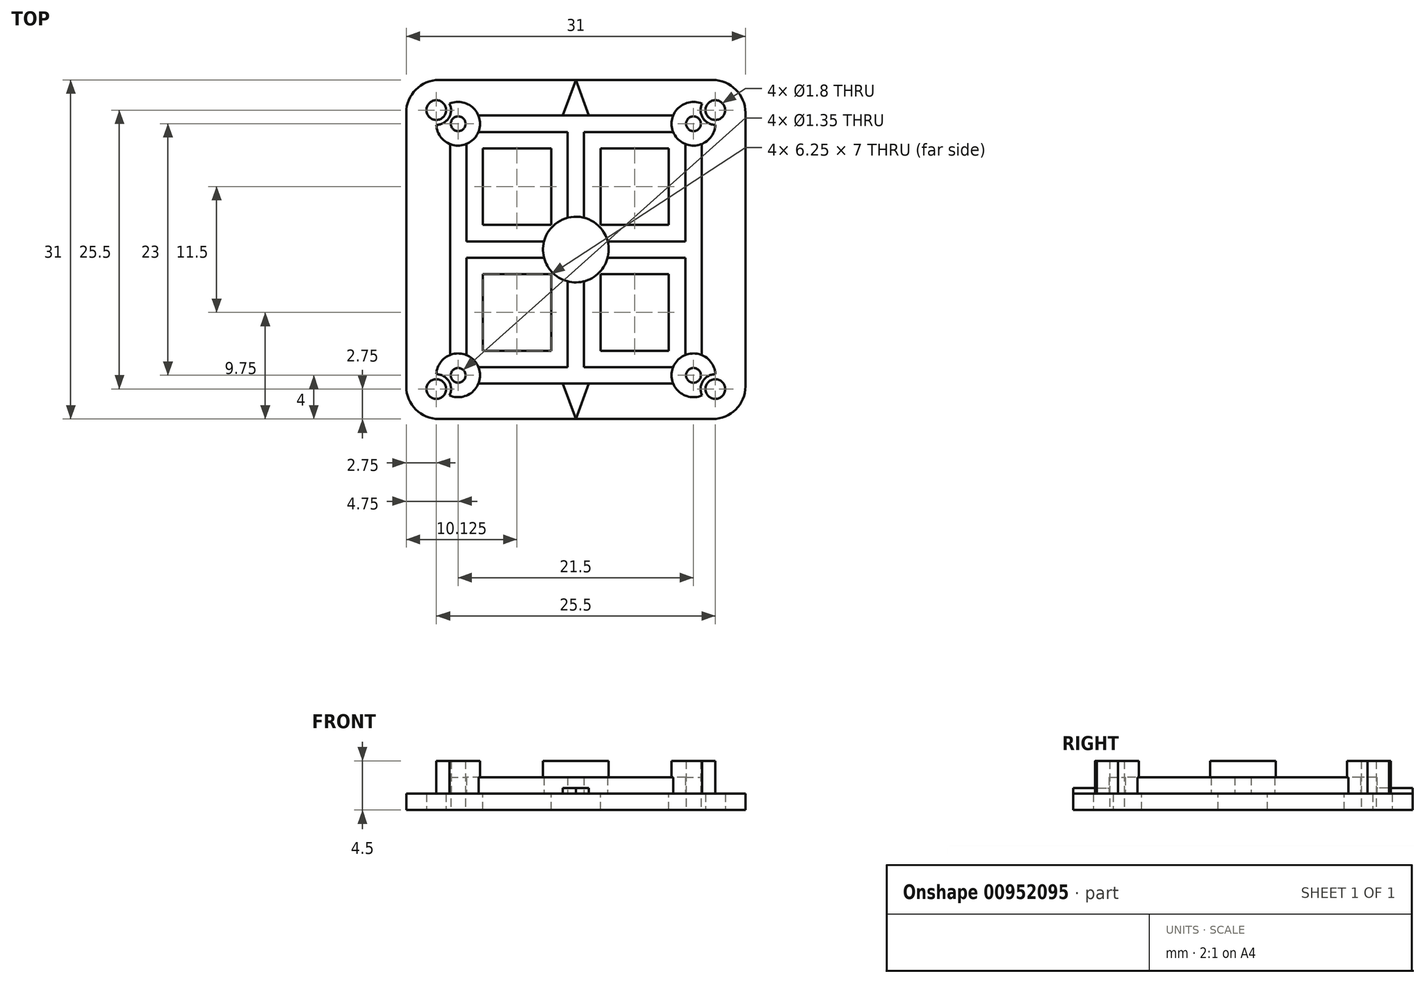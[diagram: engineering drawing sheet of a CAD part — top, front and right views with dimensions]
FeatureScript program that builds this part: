
annotation { "Feature Type Name" : "Feature", "Feature Type Description" : "" }
export const myFeature = defineFeature(function(context is Context, id is Id, definition is map)
    precondition{}
    {
        {
            var Q0;
            Q0=qCreatedBy(makeId("Top.planeOp"),FACE);
            var sketch = newSketch(context, id + "F0", { "sketchPlane" : qUnion([Q0])});
            skCircle(sketch, "E0", {"center": v(-12.75, 12.75) * mm, "radius": 0.9 * mm});
            skCircle(sketch, "E1.MirrorC", {"center": v(12.75, 12.75) * mm, "radius": 0.9 * mm});
            skCircle(sketch, "E2.MirrorC", {"center": v(12.75, -12.75) * mm, "radius": 0.9 * mm});
            skCircle(sketch, "E3.MirrorC", {"center": v(-12.75, -12.75) * mm, "radius": 0.9 * mm});
            skLineSegment(sketch, "E4.bottom", {"start": v(-15.5, 15.5) * mm, "end": v(15.5, 15.5) * mm});
            skLineSegment(sketch, "E4.top", {"start": v(-15.5, -15.5) * mm, "end": v(15.5, -15.5) * mm});
            skLineSegment(sketch, "E4.left", {"start": v(-15.5, 15.5) * mm, "end": v(-15.5, -15.5) * mm});
            skLineSegment(sketch, "E4.right", {"start": v(15.5, 15.5) * mm, "end": v(15.5, -15.5) * mm});
            skSolve(sketch);
        }
        {
            var Q0;
            Q0 = qSketchRegion(id + "F0", true);
            extrude(context, id + "F1", {"entities" : qUnion([Q0]), "depth" : 1.5 * mm, "offsetDistance" : 25 * mm});
        }
        {
            var Q0;
            Q0=makeQuery(id+"F1.opExtrude","CAP_FACE",FACE,{"disambiguationData":[OSD([sQuery(id+"F0.wireOp",EDGE,"E0"),sQuery(id+"F0.wireOp",EDGE,"E1.MirrorC"),sQuery(id+"F0.wireOp",EDGE,"E2.MirrorC"),sQuery(id+"F0.wireOp",EDGE,"E3.MirrorC"),sQuery(id+"F0.wireOp",EDGE,"E4.bottom"),sQuery(id+"F0.wireOp",EDGE,"E4.top"),sQuery(id+"F0.wireOp",EDGE,"E4.left"),sQuery(id+"F0.wireOp",EDGE,"E4.right")])],"isStart":false});
            var sketch = newSketch(context, id + "F2", { "sketchPlane" : qUnion([Q0])});
            skCircle(sketch, "E5", {"center": v(10.75, 11.5) * mm, "radius": 0.68 * mm});
            skCircle(sketch, "E6.MirrorC", {"center": v(-10.75, 11.5) * mm, "radius": 0.68 * mm});
            skCircle(sketch, "E7.MirrorC", {"center": v(-10.75, -11.5) * mm, "radius": 0.68 * mm});
            skCircle(sketch, "E8.MirrorC", {"center": v(10.75, -11.5) * mm, "radius": 0.68 * mm});
            skCircle(sketch, "E9", {"center": v(-10.75, 11.5) * mm, "radius": 2 * mm});
            skCircle(sketch, "E10.MirrorC", {"center": v(10.75, 11.5) * mm, "radius": 2 * mm});
            skCircle(sketch, "E11.MirrorC", {"center": v(10.75, -11.5) * mm, "radius": 2 * mm});
            skCircle(sketch, "E12.MirrorC", {"center": v(-10.75, -11.5) * mm, "radius": 2 * mm});
            skSolve(sketch);
        }
        {
            var Q0;
            Q0 = qSketchRegion(id + "F2", true);
            extrude(context, id + "F3", {"entities" : qUnion([Q0]), "operationType" : NewBodyOperationType.ADD, "depth" : 3 * mm, "offsetDistance" : 25 * mm});
        }
        {
            var Q0;
            Q0=makeQuery(id+"F1.opExtrude","SWEPT_EDGE",EDGE,{"disambiguationData":[OSD([sQuery(id+"F0.wireOp",EDGE,"E4.bottom"),sQuery(id+"F0.wireOp",EDGE,"E4.left")])]});
            var Q1;
            Q1=makeQuery(id+"F1.opExtrude","SWEPT_EDGE",EDGE,{"disambiguationData":[OSD([sQuery(id+"F0.wireOp",EDGE,"E4.bottom"),sQuery(id+"F0.wireOp",EDGE,"E4.right")])]});
            var Q2;
            Q2=makeQuery(id+"F1.opExtrude","SWEPT_EDGE",EDGE,{"disambiguationData":[OSD([sQuery(id+"F0.wireOp",EDGE,"E4.top"),sQuery(id+"F0.wireOp",EDGE,"E4.right")])]});
            var Q3;
            Q3=makeQuery(id+"F1.opExtrude","SWEPT_EDGE",EDGE,{"disambiguationData":[OSD([sQuery(id+"F0.wireOp",EDGE,"E4.top"),sQuery(id+"F0.wireOp",EDGE,"E4.left")])]});
            fillet(context, id + "F4", {"entities" : qUnion([Q0, Q1, Q2, Q3]), "radius" : 3 * mm, "tangentPropagation" : true, "allowEdgeOverflow" : false});
        }
        {
            var Q0;
            {var subQ1=sQuery(id+"F0.wireOp",EDGE,"E3.MirrorC");var subQ2=sQuery(id+"F0.wireOp",EDGE,"E4.right");var subQ3=sQuery(id+"F0.wireOp",EDGE,"E4.left");var subQ5=sQuery(id+"F0.wireOp",EDGE,"E4.top");var subQ6=sQuery(id+"F0.wireOp",EDGE,"E4.bottom");var subQ7=sQuery(id+"F0.wireOp",EDGE,"E0");var subQ8=sQuery(id+"F0.wireOp",EDGE,"E1.MirrorC");var subQ9=sQuery(id+"F0.wireOp",EDGE,"E2.MirrorC");Q0=makeQuery(id+"F3.boolean.opBoolean","SPLIT",FACE,{"disambiguationData":[TD([makeQuery(id+"F1.opExtrude","SWEPT_FACE",FACE,{"disambiguationData":[OSD([subQ7])]})])],"derivedFrom":makeQuery(id+"F1.opExtrude","CAP_FACE",FACE,{"disambiguationData":[OSD([subQ7,subQ8,subQ9,subQ1,subQ6,subQ5,subQ3,subQ2])],"isStart":false})});}
            var sketch = newSketch(context, id + "F5", { "sketchPlane" : qUnion([Q0])});
            skLineSegment(sketch, "E13.bottom", {"start": v(-8.9, -10.75) * mm, "end": v(8.9, -10.75) * mm});
            skLineSegment(sketch, "E13.top", {"start": v(-8.9, -12.25) * mm, "end": v(8.9, -12.25) * mm});
            skLineSegment(sketch, "E13.left", {"start": v(-8.9, -10.75) * mm, "end": v(-8.9, -12.25) * mm});
            skLineSegment(sketch, "E13.right", {"start": v(8.9, -10.75) * mm, "end": v(8.9, -12.25) * mm});
            skLineSegment(sketch, "E14.bottom", {"start": v(-8.9, 12.25) * mm, "end": v(8.9, 12.25) * mm});
            skLineSegment(sketch, "E14.top", {"start": v(-8.9, 10.75) * mm, "end": v(8.9, 10.75) * mm});
            skLineSegment(sketch, "E14.left", {"start": v(-8.9, 12.25) * mm, "end": v(-8.9, 10.75) * mm});
            skLineSegment(sketch, "E14.right", {"start": v(8.9, 12.25) * mm, "end": v(8.9, 10.75) * mm});
            skLineSegment(sketch, "E15.bottom", {"start": v(-11.5, 9.65) * mm, "end": v(-10, 9.65) * mm});
            skLineSegment(sketch, "E15.top", {"start": v(-11.5, -9.65) * mm, "end": v(-10, -9.65) * mm});
            skLineSegment(sketch, "E15.left", {"start": v(-11.5, 9.65) * mm, "end": v(-11.5, -9.65) * mm});
            skLineSegment(sketch, "E15.right", {"start": v(-10, 9.65) * mm, "end": v(-10, -9.65) * mm});
            skLineSegment(sketch, "E16.MirrorCS", {"start": v(10, 9.65) * mm, "end": v(10, -9.65) * mm});
            skLineSegment(sketch, "E17.MirrorCS", {"start": v(11.5, 9.65) * mm, "end": v(11.5, -9.65) * mm});
            skLineSegment(sketch, "E18.MirrorCS", {"start": v(11.5, -9.65) * mm, "end": v(10, -9.65) * mm});
            skLineSegment(sketch, "E19.MirrorCS", {"start": v(11.5, 9.65) * mm, "end": v(10, 9.65) * mm});
            skLineSegment(sketch, "E20.bottom", {"start": v(-0.75, 10.75) * mm, "end": v(0.75, 10.75) * mm});
            skLineSegment(sketch, "E20.top", {"start": v(-0.75, -10.75) * mm, "end": v(0.75, -10.75) * mm});
            skLineSegment(sketch, "E20.left", {"start": v(-0.75, 10.75) * mm, "end": v(-0.75, 0.75) * mm});
            skLineSegment(sketch, "E20.right", {"start": v(0.75, 10.75) * mm, "end": v(0.75, 0.75) * mm});
            skLineSegment(sketch, "E21", {"start": v(-0.75, 0.75) * mm, "end": v(-10, 0.75) * mm});
            skLineSegment(sketch, "E22", {"start": v(-10, 0.75) * mm, "end": v(-10, -0.75) * mm});
            skLineSegment(sketch, "E23", {"start": v(-10, -0.75) * mm, "end": v(-0.75, -0.75) * mm});
            skLineSegment(sketch, "E24.MirrorCS", {"start": v(10, 0.75) * mm, "end": v(10, -0.75) * mm});
            skLineSegment(sketch, "E25.MirrorCS", {"start": v(0.75, 0.75) * mm, "end": v(10, 0.75) * mm});
            skLineSegment(sketch, "E26.MirrorCS", {"start": v(10, -0.75) * mm, "end": v(0.75, -0.75) * mm});
            skLineSegment(sketch, "E27.trimOffspring", {"start": v(-0.75, -0.75) * mm, "end": v(-0.75, -10.75) * mm});
            skLineSegment(sketch, "E28.trimOffspring", {"start": v(0.75, -0.75) * mm, "end": v(0.75, -10.75) * mm});
            skSolve(sketch);
        }
        {
            var Q0;
            Q0 = qSketchRegion(id + "F5", true);
            extrude(context, id + "F6", {"entities" : qUnion([Q0]), "operationType" : NewBodyOperationType.ADD, "depth" : 1.5 * mm, "offsetDistance" : 25 * mm});
        }
        {
            var Q0;
            {var subQ1=sQuery(id+"F0.wireOp",EDGE,"E4.right");var subQ2=sQuery(id+"F0.wireOp",EDGE,"E4.left");var subQ3=sQuery(id+"F0.wireOp",EDGE,"E4.top");var subQ4=sQuery(id+"F0.wireOp",EDGE,"E4.bottom");var subQ5=sQuery(id+"F0.wireOp",EDGE,"E3.MirrorC");var subQ6=sQuery(id+"F0.wireOp",EDGE,"E2.MirrorC");var subQ7=sQuery(id+"F0.wireOp",EDGE,"E1.MirrorC");var subQ8=sQuery(id+"F0.wireOp",EDGE,"E0");var subQ9=makeQuery(id+"F1.opExtrude","CAP_FACE",FACE,{"disambiguationData":[OSD([subQ8,subQ7,subQ6,subQ5,subQ4,subQ3,subQ2,subQ1])],"isStart":false});var subQ15=sQuery(id+"F5.wireOp",EDGE,"E20.left");Q0=makeQuery(id+"F6.boolean.opBoolean","SPLIT",FACE,{"disambiguationData":[TD([makeQuery(id+"F6.opExtrude","SWEPT_FACE",FACE,{"disambiguationData":[OSD([subQ15])]})])],"derivedFrom":makeQuery(id+"F3.boolean.opBoolean","SPLIT",FACE,{"disambiguationData":[TD([makeQuery(id+"F1.opExtrude","SWEPT_FACE",FACE,{"disambiguationData":[OSD([subQ8])]})])],"derivedFrom":subQ9})});}
            var sketch = newSketch(context, id + "F7", { "sketchPlane" : qUnion([Q0])});
            skLineSegment(sketch, "E29.bottom", {"start": v(-8.5, 9.25) * mm, "end": v(-2.25, 9.25) * mm});
            skLineSegment(sketch, "E29.top", {"start": v(-8.5, 2.25) * mm, "end": v(-2.25, 2.25) * mm});
            skLineSegment(sketch, "E29.left", {"start": v(-8.5, 9.25) * mm, "end": v(-8.5, 2.25) * mm});
            skLineSegment(sketch, "E29.right", {"start": v(-2.25, 9.25) * mm, "end": v(-2.25, 2.25) * mm});
            skLineSegment(sketch, "E30.MirrorCS", {"start": v(8.5, 9.25) * mm, "end": v(2.25, 9.25) * mm});
            skLineSegment(sketch, "E31.MirrorCS", {"start": v(8.5, 9.25) * mm, "end": v(8.5, 2.25) * mm});
            skLineSegment(sketch, "E32.MirrorCS", {"start": v(8.5, 2.25) * mm, "end": v(2.25, 2.25) * mm});
            skLineSegment(sketch, "E33.MirrorCS", {"start": v(2.25, 9.25) * mm, "end": v(2.25, 2.25) * mm});
            skLineSegment(sketch, "E34.MirrorCS", {"start": v(2.25, -9.25) * mm, "end": v(2.25, -2.25) * mm});
            skLineSegment(sketch, "E35.MirrorCS", {"start": v(-8.5, -9.25) * mm, "end": v(-2.25, -9.25) * mm});
            skLineSegment(sketch, "E36.MirrorCS", {"start": v(8.5, -9.25) * mm, "end": v(2.25, -9.25) * mm});
            skLineSegment(sketch, "E37.MirrorCS", {"start": v(8.5, -9.25) * mm, "end": v(8.5, -2.25) * mm});
            skLineSegment(sketch, "E38.MirrorCS", {"start": v(-8.5, -2.25) * mm, "end": v(-2.25, -2.25) * mm});
            skLineSegment(sketch, "E39.MirrorCS", {"start": v(-2.25, -9.25) * mm, "end": v(-2.25, -2.25) * mm});
            skLineSegment(sketch, "E40.MirrorCS", {"start": v(8.5, -2.25) * mm, "end": v(2.25, -2.25) * mm});
            skLineSegment(sketch, "E41.MirrorCS", {"start": v(-8.5, -9.25) * mm, "end": v(-8.5, -2.25) * mm});
            skSolve(sketch);
        }
        {
            var Q0;
            Q0 = qSketchRegion(id + "F7", true);
            extrude(context, id + "F8", {"entities" : qUnion([Q0]), "operationType" : NewBodyOperationType.REMOVE, "oppositeDirection" : true, "depth" : 25 * mm, "offsetDistance" : 25 * mm});
        }
        {
            var Q0;
            {var subQ1=sQuery(id+"F0.wireOp",EDGE,"E4.right");var subQ2=sQuery(id+"F0.wireOp",EDGE,"E4.left");var subQ3=sQuery(id+"F0.wireOp",EDGE,"E4.top");var subQ4=sQuery(id+"F0.wireOp",EDGE,"E4.bottom");var subQ5=sQuery(id+"F0.wireOp",EDGE,"E3.MirrorC");var subQ6=sQuery(id+"F0.wireOp",EDGE,"E2.MirrorC");var subQ7=sQuery(id+"F0.wireOp",EDGE,"E1.MirrorC");var subQ8=sQuery(id+"F0.wireOp",EDGE,"E0");var subQ9=makeQuery(id+"F1.opExtrude","CAP_FACE",FACE,{"disambiguationData":[OSD([subQ8,subQ7,subQ6,subQ5,subQ4,subQ3,subQ2,subQ1])],"isStart":false});var subQ13=sQuery(id+"F5.wireOp",EDGE,"E23");Q0=makeQuery(id+"F6.boolean.opBoolean","SPLIT",FACE,{"disambiguationData":[TD([makeQuery(id+"F6.opExtrude","SWEPT_FACE",FACE,{"disambiguationData":[OSD([subQ13])]})])],"derivedFrom":makeQuery(id+"F3.boolean.opBoolean","SPLIT",FACE,{"disambiguationData":[TD([makeQuery(id+"F1.opExtrude","SWEPT_FACE",FACE,{"disambiguationData":[OSD([subQ8])]})])],"derivedFrom":subQ9})});}
            var sketch = newSketch(context, id + "F9", { "sketchPlane" : qUnion([Q0])});
            skCircle(sketch, "E42", {"center": v(0, 0) * mm, "radius": 3 * mm});
            skSolve(sketch);
        }
        {
            var Q0;
            Q0 = qSketchRegion(id + "F9", true);
            var Q1;
            Q1=makeQuery(id+"F3.opExtrude","CAP_FACE",FACE,{"disambiguationData":[OSD([sQuery(id+"F2.wireOp",EDGE,"E7.MirrorC"),sQuery(id+"F2.wireOp",EDGE,"E12.MirrorC")])],"isStart":false});
            extrude(context, id + "F10", {"entities" : qUnion([Q0]), "operationType" : NewBodyOperationType.ADD, "endBound" : BoundingType.UP_TO_SURFACE, "depth" : 25 * mm, "endBoundEntityFace" : qUnion([Q1]), "offsetDistance" : 25 * mm});
        }
        {
            var Q0;
            Q0=makeQuery(id+"F3.opExtrude","CAP_FACE",FACE,{"disambiguationData":[OSD([sQuery(id+"F2.wireOp",EDGE,"E7.MirrorC"),sQuery(id+"F2.wireOp",EDGE,"E12.MirrorC")])],"isStart":true});
            var Q1;
            Q1=makeQuery(id+"F3.opExtrude","CAP_FACE",FACE,{"disambiguationData":[OSD([sQuery(id+"F2.wireOp",EDGE,"E6.MirrorC"),sQuery(id+"F2.wireOp",EDGE,"E9")])],"isStart":true});
            var Q2;
            Q2=makeQuery(id+"F3.opExtrude","CAP_FACE",FACE,{"disambiguationData":[OSD([sQuery(id+"F2.wireOp",EDGE,"E5"),sQuery(id+"F2.wireOp",EDGE,"E10.MirrorC")])],"isStart":true});
            var Q3;
            Q3=makeQuery(id+"F3.opExtrude","CAP_FACE",FACE,{"disambiguationData":[OSD([sQuery(id+"F2.wireOp",EDGE,"E8.MirrorC"),sQuery(id+"F2.wireOp",EDGE,"E11.MirrorC")])],"isStart":true});
            extrude(context, id + "F11", {"entities" : qUnion([Q0, Q1, Q2, Q3]), "operationType" : NewBodyOperationType.REMOVE, "oppositeDirection" : true, "depth" : 25 * mm, "offsetDistance" : 25 * mm});
        }
        {
            var Q0;
            {var subQ0=sQuery(id+"F0.wireOp",EDGE,"E4.right");var subQ1=sQuery(id+"F0.wireOp",EDGE,"E4.top");var subQ2=sQuery(id+"F0.wireOp",EDGE,"E4.left");var subQ3=sQuery(id+"F0.wireOp",EDGE,"E4.bottom");var subQ14=sQuery(id+"F0.wireOp",EDGE,"E2.MirrorC");var subQ16=sQuery(id+"F0.wireOp",EDGE,"E1.MirrorC");var subQ19=sQuery(id+"F0.wireOp",EDGE,"E0");var subQ20=makeQuery(id+"F1.opExtrude","SWEPT_FACE",FACE,{"disambiguationData":[OSD([subQ19])]});var subQ25=sQuery(id+"F0.wireOp",EDGE,"E3.MirrorC");Q0=makeQuery(id+"F6.boolean.opBoolean","SPLIT",FACE,{"disambiguationData":[TD([subQ20])],"derivedFrom":makeQuery(id+"F3.boolean.opBoolean","SPLIT",FACE,{"disambiguationData":[TD([subQ20])],"derivedFrom":makeQuery(id+"F1.opExtrude","CAP_FACE",FACE,{"disambiguationData":[OSD([subQ19,subQ16,subQ14,subQ25,subQ3,subQ1,subQ2,subQ0])],"isStart":false})})});}
            var sketch = newSketch(context, id + "F12", { "sketchPlane" : qUnion([Q0])});
            skCircle(sketch, "E43", {"center": v(-12.75, -12.75) * mm, "radius": 1.35 * mm});
            skCircle(sketch, "E44.MirrorC", {"center": v(12.75, -12.75) * mm, "radius": 1.35 * mm});
            skCircle(sketch, "E45.MirrorC", {"center": v(-12.75, 12.75) * mm, "radius": 1.35 * mm});
            skCircle(sketch, "E46.MirrorC", {"center": v(12.75, 12.75) * mm, "radius": 1.35 * mm});
            skSolve(sketch);
        }
        {
            var Q0;
            Q0 = qSketchRegion(id + "F12", true);
            extrude(context, id + "F13", {"entities" : qUnion([Q0]), "operationType" : NewBodyOperationType.REMOVE, "depth" : 25 * mm, "offsetDistance" : 25 * mm});
        }
        {
            var Q0;
            Q0=makeQuery(id+"F3.boolean.opBoolean","SPLIT",FACE,{"disambiguationData":[TD([makeQuery(id+"F3.opExtrude","SWEPT_FACE",FACE,{"disambiguationData":[OSD([sQuery(id+"F2.wireOp",EDGE,"E5")])]})])],"derivedFrom":makeQuery(id+"F1.opExtrude","CAP_FACE",FACE,{"disambiguationData":[OSD([sQuery(id+"F0.wireOp",EDGE,"E0"),sQuery(id+"F0.wireOp",EDGE,"E1.MirrorC"),sQuery(id+"F0.wireOp",EDGE,"E2.MirrorC"),sQuery(id+"F0.wireOp",EDGE,"E3.MirrorC"),sQuery(id+"F0.wireOp",EDGE,"E4.bottom"),sQuery(id+"F0.wireOp",EDGE,"E4.top"),sQuery(id+"F0.wireOp",EDGE,"E4.left"),sQuery(id+"F0.wireOp",EDGE,"E4.right")])],"isStart":false})});
            var Q1;
            Q1=makeQuery(id+"F3.boolean.opBoolean","SPLIT",FACE,{"disambiguationData":[TD([makeQuery(id+"F3.opExtrude","SWEPT_FACE",FACE,{"disambiguationData":[OSD([sQuery(id+"F2.wireOp",EDGE,"E6.MirrorC")])]})])],"derivedFrom":makeQuery(id+"F1.opExtrude","CAP_FACE",FACE,{"disambiguationData":[OSD([sQuery(id+"F0.wireOp",EDGE,"E0"),sQuery(id+"F0.wireOp",EDGE,"E1.MirrorC"),sQuery(id+"F0.wireOp",EDGE,"E2.MirrorC"),sQuery(id+"F0.wireOp",EDGE,"E3.MirrorC"),sQuery(id+"F0.wireOp",EDGE,"E4.bottom"),sQuery(id+"F0.wireOp",EDGE,"E4.top"),sQuery(id+"F0.wireOp",EDGE,"E4.left"),sQuery(id+"F0.wireOp",EDGE,"E4.right")])],"isStart":false})});
            var Q2;
            Q2=makeQuery(id+"F3.boolean.opBoolean","SPLIT",FACE,{"disambiguationData":[TD([makeQuery(id+"F3.opExtrude","SWEPT_FACE",FACE,{"disambiguationData":[OSD([sQuery(id+"F2.wireOp",EDGE,"E7.MirrorC")])]})])],"derivedFrom":makeQuery(id+"F1.opExtrude","CAP_FACE",FACE,{"disambiguationData":[OSD([sQuery(id+"F0.wireOp",EDGE,"E0"),sQuery(id+"F0.wireOp",EDGE,"E1.MirrorC"),sQuery(id+"F0.wireOp",EDGE,"E2.MirrorC"),sQuery(id+"F0.wireOp",EDGE,"E3.MirrorC"),sQuery(id+"F0.wireOp",EDGE,"E4.bottom"),sQuery(id+"F0.wireOp",EDGE,"E4.top"),sQuery(id+"F0.wireOp",EDGE,"E4.left"),sQuery(id+"F0.wireOp",EDGE,"E4.right")])],"isStart":false})});
            var Q3;
            Q3=makeQuery(id+"F3.boolean.opBoolean","SPLIT",FACE,{"disambiguationData":[TD([makeQuery(id+"F3.opExtrude","SWEPT_FACE",FACE,{"disambiguationData":[OSD([sQuery(id+"F2.wireOp",EDGE,"E8.MirrorC")])]})])],"derivedFrom":makeQuery(id+"F1.opExtrude","CAP_FACE",FACE,{"disambiguationData":[OSD([sQuery(id+"F0.wireOp",EDGE,"E0"),sQuery(id+"F0.wireOp",EDGE,"E1.MirrorC"),sQuery(id+"F0.wireOp",EDGE,"E2.MirrorC"),sQuery(id+"F0.wireOp",EDGE,"E3.MirrorC"),sQuery(id+"F0.wireOp",EDGE,"E4.bottom"),sQuery(id+"F0.wireOp",EDGE,"E4.top"),sQuery(id+"F0.wireOp",EDGE,"E4.left"),sQuery(id+"F0.wireOp",EDGE,"E4.right")])],"isStart":false})});
            extrude(context, id + "F14", {"entities" : qUnion([Q0, Q1, Q2, Q3]), "operationType" : NewBodyOperationType.REMOVE, "oppositeDirection" : true, "depth" : 25 * mm, "offsetDistance" : 25 * mm});
        }
        {
            var Q0;
            {var subQ0=sQuery(id+"F0.wireOp",EDGE,"E4.right");var subQ1=sQuery(id+"F0.wireOp",EDGE,"E4.top");var subQ2=sQuery(id+"F0.wireOp",EDGE,"E4.left");var subQ3=sQuery(id+"F0.wireOp",EDGE,"E4.bottom");var subQ14=sQuery(id+"F0.wireOp",EDGE,"E2.MirrorC");var subQ16=sQuery(id+"F0.wireOp",EDGE,"E1.MirrorC");var subQ19=sQuery(id+"F0.wireOp",EDGE,"E0");var subQ20=makeQuery(id+"F1.opExtrude","SWEPT_FACE",FACE,{"disambiguationData":[OSD([subQ19])]});var subQ25=sQuery(id+"F0.wireOp",EDGE,"E3.MirrorC");Q0=makeQuery(id+"F13.boolean.opBoolean","MERGE",FACE,{"derivedFrom":[makeQuery(id+"F6.boolean.opBoolean","SPLIT",FACE,{"disambiguationData":[TD([subQ20])],"derivedFrom":makeQuery(id+"F3.boolean.opBoolean","SPLIT",FACE,{"disambiguationData":[TD([subQ20])],"derivedFrom":makeQuery(id+"F1.opExtrude","CAP_FACE",FACE,{"disambiguationData":[OSD([subQ19,subQ16,subQ14,subQ25,subQ3,subQ1,subQ2,subQ0])],"isStart":false})})})],"fromTools":[makeQuery(id+"F13.opExtrude","CAP_FACE",FACE,{"disambiguationData":[OSD([sQuery(id+"F12.wireOp",EDGE,"E43")])],"isStart":true}),makeQuery(id+"F13.opExtrude","CAP_FACE",FACE,{"disambiguationData":[OSD([sQuery(id+"F12.wireOp",EDGE,"E44.MirrorC")])],"isStart":true}),makeQuery(id+"F13.opExtrude","CAP_FACE",FACE,{"disambiguationData":[OSD([sQuery(id+"F12.wireOp",EDGE,"E45.MirrorC")])],"isStart":true}),makeQuery(id+"F13.opExtrude","CAP_FACE",FACE,{"disambiguationData":[OSD([sQuery(id+"F12.wireOp",EDGE,"E46.MirrorC")])],"isStart":true})]});}
            var sketch = newSketch(context, id + "F15", { "sketchPlane" : qUnion([Q0])});
            skLineSegment(sketch, "E47", {"start": v(0, 15.5) * mm, "end": v(-1.18, 12.25) * mm});
            skLineSegment(sketch, "E48", {"start": v(-1.18, 12.25) * mm, "end": v(0, 12.25) * mm});
            skLineSegment(sketch, "E49.MirrorCS", {"start": v(0, 15.5) * mm, "end": v(1.18, 12.25) * mm});
            skLineSegment(sketch, "E50.MirrorCS", {"start": v(1.18, 12.25) * mm, "end": v(0, 12.25) * mm});
            skLineSegment(sketch, "E51.MirrorCS", {"start": v(0, -15.5) * mm, "end": v(1.18, -12.25) * mm});
            skLineSegment(sketch, "E52.MirrorCS", {"start": v(-1.18, -12.25) * mm, "end": v(0, -12.25) * mm});
            skLineSegment(sketch, "E53.MirrorCS", {"start": v(0, -15.5) * mm, "end": v(-1.18, -12.25) * mm});
            skLineSegment(sketch, "E54.MirrorCS", {"start": v(1.18, -12.25) * mm, "end": v(0, -12.25) * mm});
            skSolve(sketch);
        }
        {
            var Q0;
            Q0 = qSketchRegion(id + "F15", true);
            extrude(context, id + "F16", {"entities" : qUnion([Q0]), "operationType" : NewBodyOperationType.ADD, "depth" : 0.5 * mm, "offsetDistance" : 25 * mm});
        }
    });
